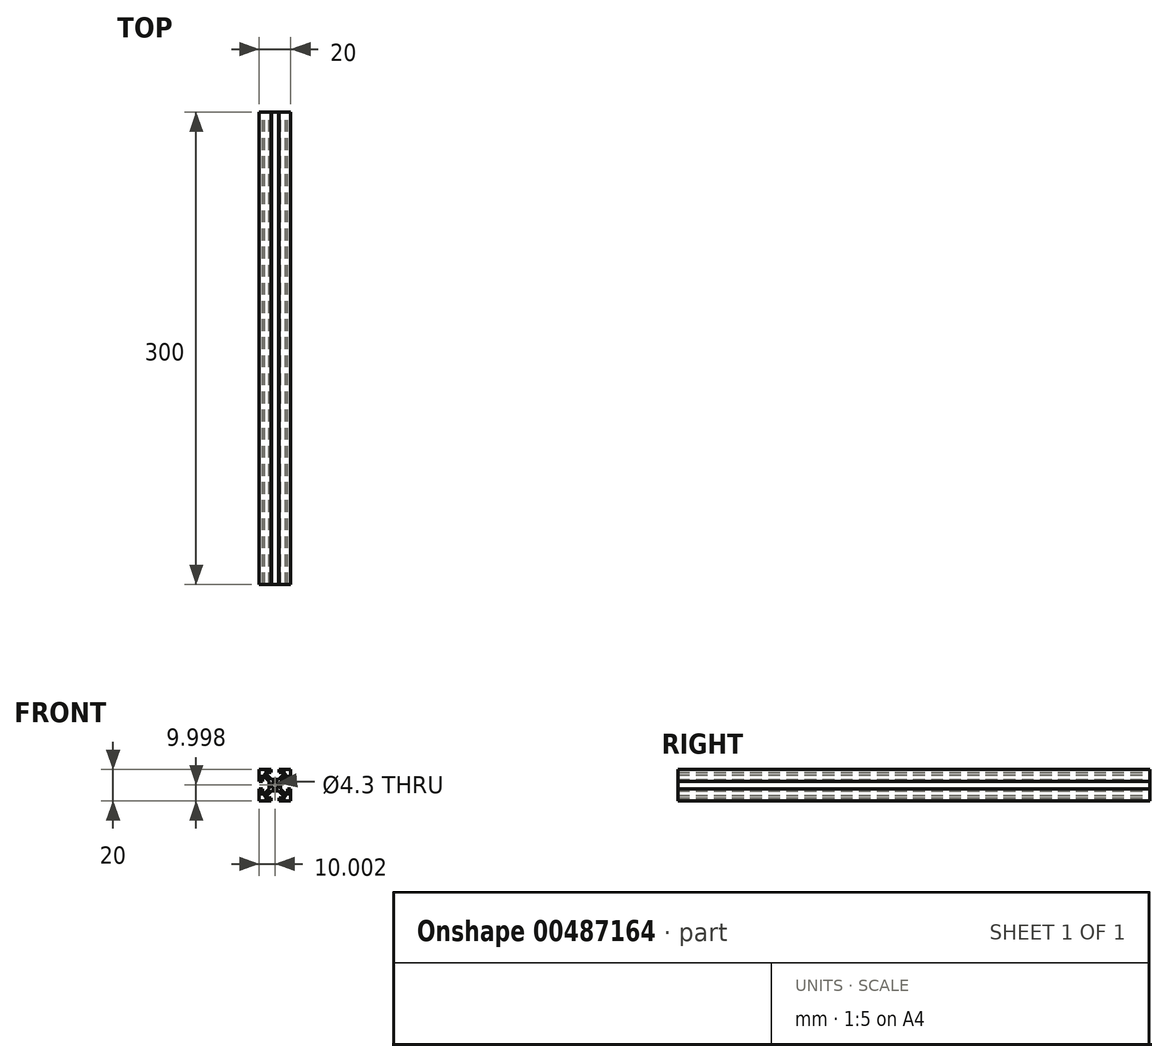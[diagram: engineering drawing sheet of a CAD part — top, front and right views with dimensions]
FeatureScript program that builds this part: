
annotation { "Feature Type Name" : "Feature", "Feature Type Description" : "" }
export const myFeature = defineFeature(function(context is Context, id is Id, definition is map)
    precondition{}
    {
        {
            var Q0;
            Q0=qCreatedBy(makeId("Front.planeOp"),FACE);
            var sketch = newSketch(context, id + "F0", { "sketchPlane" : qUnion([Q0])});
            skLineSegment(sketch, "E0.bottom", {"start": v(-9.74, 9.77) * mm, "end": v(-2.24, 9.77) * mm});
            skLineSegment(sketch, "E0.left", {"start": v(-9.74, 9.77) * mm, "end": v(-9.74, 2.27) * mm});
            skLineSegment(sketch, "E0.right", {"start": v(10.26, 9.77) * mm, "end": v(10.26, 2.27) * mm});
            skArc(sketch, "E1", {"start": v(2.41, -0.23) * mm, "mid": v(0.26, 1.92) * mm, "end": v(-1.89, -0.23) * mm});
            skLineSegment(sketch, "E2.bottom", {"start": v(-1.97, 3.42) * mm, "end": v(2.5, 3.42) * mm});
            skLineSegment(sketch, "E2.left", {"start": v(-3.39, 2) * mm, "end": v(-3.39, -0.23) * mm});
            skLineSegment(sketch, "E2.right", {"start": v(3.91, 2) * mm, "end": v(3.91, -0.23) * mm});
            skLineSegment(sketch, "E3", {"start": v(-2.24, 9.77) * mm, "end": v(-2.24, 7.77) * mm});
            skLineSegment(sketch, "E4", {"start": v(-2.24, 7.77) * mm, "end": v(-6.32, 7.77) * mm});
            skLineSegment(sketch, "E5", {"start": v(2.76, 9.77) * mm, "end": v(2.76, 7.77) * mm});
            skPoint(sketch, "E5.endSnap0", {"position": v(-5.99, 7.77) * mm});
            skLineSegment(sketch, "E6", {"start": v(2.76, 7.77) * mm, "end": v(6.85, 7.77) * mm});
            skLineSegment(sketch, "E7", {"start": v(-7.74, 6.35) * mm, "end": v(-7.74, 2.27) * mm});
            skLineSegment(sketch, "E8", {"start": v(-7.74, 2.27) * mm, "end": v(-9.74, 2.27) * mm});
            skLineSegment(sketch, "E9", {"start": v(-7.74, 6.35) * mm, "end": v(-3.39, 2) * mm});
            skLineSegment(sketch, "E10", {"start": v(-1.97, 3.42) * mm, "end": v(-6.32, 7.77) * mm});
            skPoint(sketch, "E10.endSnap0", {"position": v(-6.32, -0.18) * mm});
            skLineSegment(sketch, "E11", {"start": v(8.26, 6.35) * mm, "end": v(8.26, 2.27) * mm});
            skLineSegment(sketch, "E12", {"start": v(8.26, 2.27) * mm, "end": v(10.26, 2.27) * mm});
            skPoint(sketch, "E13.orphan", {"position": v(10.26, 7.77) * mm});
            skLineSegment(sketch, "E14", {"start": v(2.5, 3.42) * mm, "end": v(6.85, 7.77) * mm});
            skLineSegment(sketch, "E15", {"start": v(3.91, 2) * mm, "end": v(8.26, 6.35) * mm});
            skPoint(sketch, "E16.orphan", {"position": v(-9.74, 7.77) * mm});
            skPoint(sketch, "E17.orphan", {"position": v(-3.39, 3.42) * mm});
            skPoint(sketch, "E18.orphan", {"position": v(3.91, 3.42) * mm});
            skLineSegment(sketch, "E19", {"start": v(-9.74, -0.23) * mm, "end": v(10.26, -0.23) * mm, "construction": true});
            skPoint(sketch, "E0.top.end.orphan", {"position": v(10.26, -10.23) * mm});
            skPoint(sketch, "E0.top.start.orphan", {"position": v(-9.74, -10.23) * mm});
            skLineSegment(sketch, "E20.MirrorCS", {"start": v(-9.74, -10.23) * mm, "end": v(-9.74, -2.73) * mm});
            skLineSegment(sketch, "E21.MirrorCS", {"start": v(-7.74, -2.73) * mm, "end": v(-9.74, -2.73) * mm});
            skLineSegment(sketch, "E22.MirrorCS", {"start": v(-7.74, -6.82) * mm, "end": v(-7.74, -2.73) * mm});
            skLineSegment(sketch, "E23.MirrorCS", {"start": v(-7.74, -6.82) * mm, "end": v(-3.39, -2.47) * mm});
            skLineSegment(sketch, "E24.MirrorCS", {"start": v(-3.39, -2.47) * mm, "end": v(-3.39, -0.23) * mm});
            skArc(sketch, "E25.MirrorCS", {"start": v(2.41, -0.23) * mm, "mid": v(0.26, -2.38) * mm, "end": v(-1.89, -0.23) * mm});
            skLineSegment(sketch, "E26.MirrorCS", {"start": v(-1.97, -3.88) * mm, "end": v(-6.32, -8.23) * mm});
            skLineSegment(sketch, "E27.MirrorCS", {"start": v(-1.97, -3.88) * mm, "end": v(2.5, -3.88) * mm});
            skLineSegment(sketch, "E28.MirrorCS", {"start": v(-2.24, -8.23) * mm, "end": v(-6.32, -8.23) * mm});
            skLineSegment(sketch, "E29.MirrorCS", {"start": v(-2.24, -10.23) * mm, "end": v(-2.24, -8.23) * mm});
            skLineSegment(sketch, "E30.MirrorCS", {"start": v(-9.74, -10.23) * mm, "end": v(-2.24, -10.23) * mm});
            skLineSegment(sketch, "E31.MirrorCS", {"start": v(2.76, -10.23) * mm, "end": v(2.76, -8.23) * mm});
            skLineSegment(sketch, "E32.MirrorCS", {"start": v(2.76, -8.23) * mm, "end": v(6.85, -8.23) * mm});
            skLineSegment(sketch, "E33.MirrorCS", {"start": v(2.5, -3.88) * mm, "end": v(6.85, -8.23) * mm});
            skLineSegment(sketch, "E34.MirrorCS", {"start": v(3.91, -2.47) * mm, "end": v(8.26, -6.82) * mm});
            skLineSegment(sketch, "E35.MirrorCS", {"start": v(8.26, -6.82) * mm, "end": v(8.26, -2.73) * mm});
            skLineSegment(sketch, "E36.MirrorCS", {"start": v(8.26, -2.73) * mm, "end": v(10.26, -2.73) * mm});
            skLineSegment(sketch, "E37.MirrorCS", {"start": v(10.26, -10.23) * mm, "end": v(10.26, -2.73) * mm});
            skLineSegment(sketch, "E38.MirrorCS", {"start": v(3.91, -2.47) * mm, "end": v(3.91, -0.23) * mm});
            skLineSegment(sketch, "E39.trimOffspring", {"start": v(2.76, 9.77) * mm, "end": v(10.26, 9.77) * mm});
            skLineSegment(sketch, "E40.trimOffspring", {"start": v(2.76, -10.23) * mm, "end": v(10.26, -10.23) * mm});
            skSolve(sketch);
        }
        {
            var Q0;
            Q0=makeQuery(id+"F0.imprint","IMPRINT",FACE,{"disambiguationData":[TD([[makeQuery(id+"F0.imprint","IMPRINT",EDGE,{"derivedFrom":sQuery(id+"F0.wireOp",EDGE,"E0.bottom")}),-1.0]])]});
            extrude(context, id + "F1", {"entities" : qUnion([Q0]), "depth" : 150 * mm, "hasSecondDirection" : true, "secondDirectionOppositeDirection" : true, "secondDirectionDepth" : 150 * mm});
        }
    });
